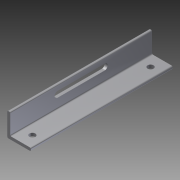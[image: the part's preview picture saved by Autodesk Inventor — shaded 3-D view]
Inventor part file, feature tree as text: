
AUTODESK INVENTOR PART (.ipt)
format: ipt  version: 2012 (Build 160160000, 160)  size: 113,664 bytes
history: native  units: in
note: dims shown in document units (in); Inventor stores cm internally (conversion verified against a paired STEP export)
features: extrude x3, sketch x3, fillet x2
ambient origin geometry x8: Origin, YZ Plane, XZ Plane, XY Plane, X Axis, Y Axis, Z Axis, Center Point
bodies: Solid1 (feature_tree)
feature tree (8):
  extrude  "Extrusion1"  Depth=0.125in
  fillet  "Fillet1"  Radius=0.125in
  fillet  "Fillet2"  Radius=1.0in
  extrude  "Extrusion2"  Depth=0.05in
  extrude  "Extrusion3"  Depth=0.25in
  sketch  "Sketch1"  dims[d1=1.0in d2=0.125in d3=0.125in d4=1.0in]
  sketch  "Sketch2"  dims[d5=6.0in d6=0.0in d7=0.05in]
  sketch  "Sketch3"  dims[d8=0.05in d9=0.25in d10=0.25in d11=0.5in d12=0.5in d13=6.0in d14=0.0in d18=6.0in d19=0.0in]
